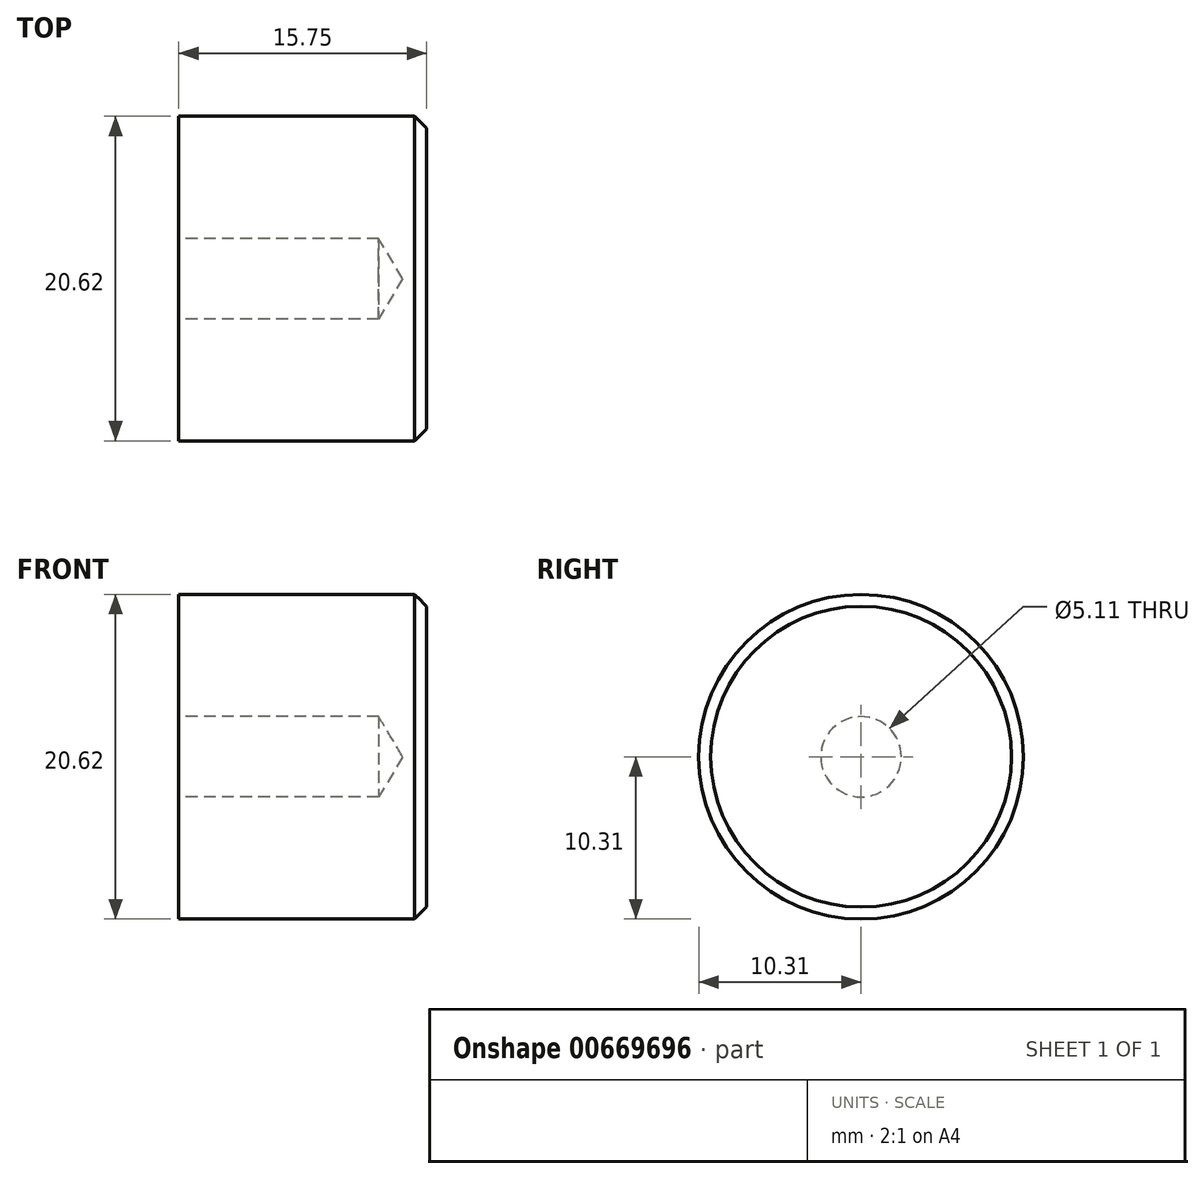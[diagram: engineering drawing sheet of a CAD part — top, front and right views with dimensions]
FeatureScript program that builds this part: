
annotation { "Feature Type Name" : "Feature", "Feature Type Description" : "" }
export const myFeature = defineFeature(function(context is Context, id is Id, definition is map)
    precondition{}
    {
        {
            var Q0;
            Q0=qCreatedBy(makeId("Front.planeOp"),FACE);
            var sketch = newSketch(context, id + "F0", { "sketchPlane" : qUnion([Q0])});
            skLineSegment(sketch, "E0.bottom", {"start": v(0, 0) * mm, "end": v(15.75, 0) * mm});
            skLineSegment(sketch, "E0.top", {"start": v(0, 10.31) * mm, "end": v(14.99, 10.31) * mm});
            skLineSegment(sketch, "E0.left", {"start": v(0, 0) * mm, "end": v(0, 10.31) * mm});
            skLineSegment(sketch, "E0.right", {"start": v(15.75, 0) * mm, "end": v(15.75, 9.55) * mm});
            skLineSegment(sketch, "E1", {"start": v(14.99, 10.31) * mm, "end": v(15.75, 9.55) * mm});
            skPoint(sketch, "E2.orphan", {"position": v(15.75, 10.31) * mm});
            skLineSegment(sketch, "E3", {"start": v(0, 0) * mm, "end": v(19.01, 0) * mm, "construction": true});
            skSolve(sketch);
        }
        {
            var Q0;
            Q0=qSketchRegion(id+"F0",true);
            var Q1;
            Q1=sQuery(id+"F0.wireOp",EDGE,"E3");
            revolve(context, id + "F1", {"entities" : qUnion([Q0]), "axis" : qUnion([Q1]), "revolveType" : RevolveType.FULL});
        }
        {
            var Q0;
            Q0=makeQuery(id+"F1.opRevolve","SWEPT_FACE",FACE,{"disambiguationData":[OSD([sQuery(id+"F0.wireOp",EDGE,"E0.left")])]});
            var sketch = newSketch(context, id + "F2", { "sketchPlane" : qUnion([Q0])});
            skPoint(sketch, "E4", {"position": v(0, 0) * mm});
            skSolve(sketch);
        }
        {
            var Q0;
            Q0=sQuery(id+"F2.wireOp",VERTEX,"E4");
            var Q1;
            Q1=makeQuery(id+"F1.opRevolve","SWEPT_BODY",BODY,{"disambiguationData":[OSD([sQuery(id+"F0.wireOp",EDGE,"E0.bottom"),sQuery(id+"F0.wireOp",EDGE,"E0.top"),sQuery(id+"F0.wireOp",EDGE,"E0.left"),sQuery(id+"F0.wireOp",EDGE,"E0.right"),sQuery(id+"F0.wireOp",EDGE,"E1")])]});
            hole(context, id + "F3", {"style" : HoleStyle.SIMPLE, "endStyle" : HoleEndStyle.BLIND, "standardTappedOrClearance" : lookupTablePath({ "standard" : "ANSI", "engagement" : "75%", "pitch" : "20 tpi", "size" : "1/4", "type" : "Tapped" }), "standardBlindInLast" : lookupTablePath({ "standard" : "ANSI", "engagement" : "75%", "pitch" : "20 tpi", "size" : "1/4", "type" : "Tapped" }), "holeDiameter" : 5.1 * mm, "majorDiameter" : 6.35 * mm, "showTappedDepth" : true, "holeDepth" : 12.7 * mm, "isTappedThrough" : true, "tappedDepth" : 8.9 * mm, "tapClearance" : 3, "locations" : qUnion([Q0]), "scope" : qUnion([Q1])});
        }
    });
